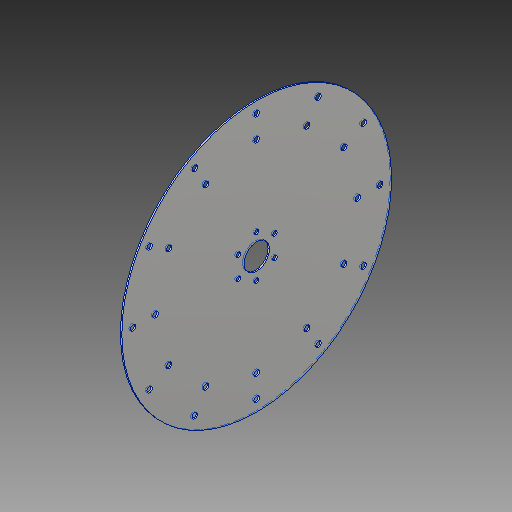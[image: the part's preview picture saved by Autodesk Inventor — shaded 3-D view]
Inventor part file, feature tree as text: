
AUTODESK INVENTOR PART (.ipt)
format: ipt  version: 2019 (Build 230136000, 136)  size: 140,288 bytes
history: native  units: in
note: dims shown in document units (in); Inventor stores cm internally (conversion verified against a paired STEP export)
features: extrude x2, sketch x2
ambient origin geometry x8: Origin, YZ Plane, XZ Plane, XY Plane, X Axis, Y Axis, Z Axis, Center Point
bodies: Solid1 (feature_tree)
feature tree (4):
  extrude  "Extrusion1"  Depth=0.5in
  extrude  "Extrusion2"  Depth=0.0625in
  sketch  "Sketch1"  dims[d0=12.0in d1=0.5in]
  sketch  "Sketch2"  dims[d2=1.0in d3=0.25in d4=4.7244in d6=360.0deg d8=0.0625in d9=0.0in d10=1.14in d11=0.204in d12=1.875in d13=2.3622in d15=360.0deg d17=1.0in d18=0.0in]
